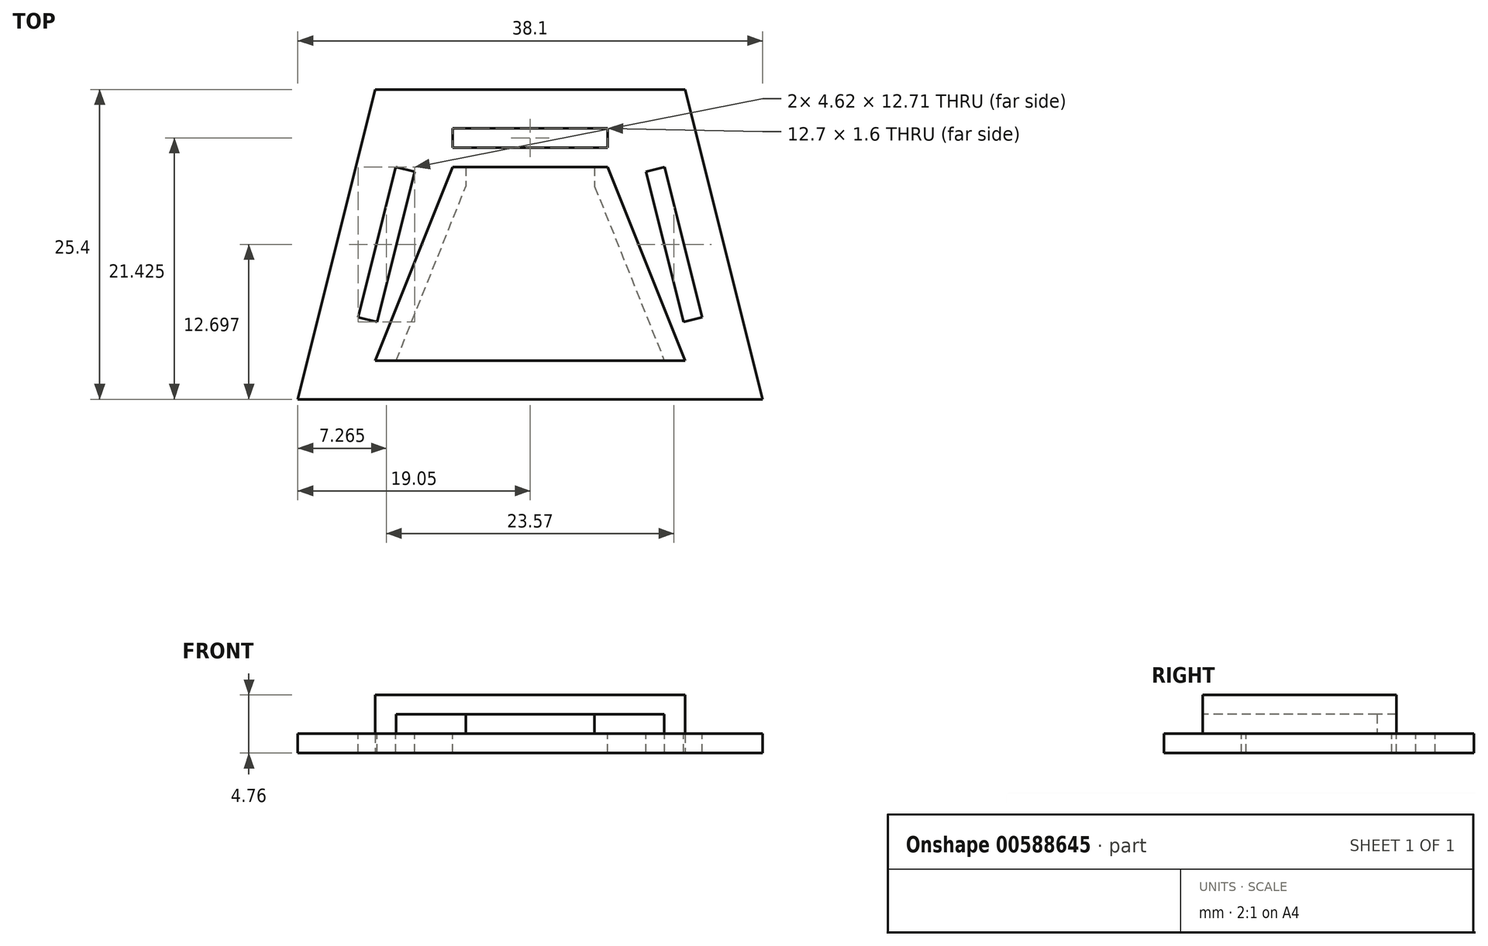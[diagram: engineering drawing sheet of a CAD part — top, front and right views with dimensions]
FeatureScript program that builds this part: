
annotation { "Feature Type Name" : "Feature", "Feature Type Description" : "" }
export const myFeature = defineFeature(function(context is Context, id is Id, definition is map)
    precondition{}
    {
        {
            var Q0;
            Q0=qCreatedBy(makeId("Top.planeOp"),FACE);
            var sketch = newSketch(context, id + "F0", { "sketchPlane" : qUnion([Q0])});
            skLineSegment(sketch, "E0", {"start": v(-19.05, -12.7) * mm, "end": v(19.05, -12.7) * mm});
            skLineSegment(sketch, "E1", {"start": v(-19.05, -12.7) * mm, "end": v(-12.7, 12.7) * mm});
            skLineSegment(sketch, "E2", {"start": v(-12.7, 12.7) * mm, "end": v(12.7, 12.7) * mm});
            skLineSegment(sketch, "E3", {"start": v(12.7, 12.7) * mm, "end": v(19.05, -12.7) * mm});
            skLineSegment(sketch, "E4", {"start": v(-19.05, -12.7) * mm, "end": v(-19.05, 12.7) * mm, "construction": true});
            skLineSegment(sketch, "E5", {"start": v(-19.05, 12.7) * mm, "end": v(-12.7, 12.7) * mm, "construction": true});
            skLineSegment(sketch, "E6", {"start": v(12.7, 12.7) * mm, "end": v(19.05, 12.7) * mm, "construction": true});
            skLineSegment(sketch, "E7", {"start": v(19.05, 12.7) * mm, "end": v(19.05, -12.7) * mm, "construction": true});
            skLineSegment(sketch, "E8", {"start": v(-19.05, -12.7) * mm, "end": v(19.05, 12.7) * mm, "construction": true});
            skPoint(sketch, "E9", {"position": v(0, 0) * mm});
            skSolve(sketch);
        }
        {
            var Q0;
            Q0 = qSketchRegion(id + "F0", true);
            extrude(context, id + "F1", {"entities" : qUnion([Q0]), "depth" : 1.59 * mm, "offsetDistance" : 25.4 * mm});
        }
        {
            var Q0;
            Q0=makeQuery(id+"F1.opExtrude","CAP_FACE",FACE,{"disambiguationData":[OSD([sQuery(id+"F0.wireOp",EDGE,"E0"),sQuery(id+"F0.wireOp",EDGE,"E1"),sQuery(id+"F0.wireOp",EDGE,"E2"),sQuery(id+"F0.wireOp",EDGE,"E3")])],"isStart":false});
            var sketch = newSketch(context, id + "F2", { "sketchPlane" : qUnion([Q0])});
            skLineSegment(sketch, "E10", {"start": v(-6.35, 6.35) * mm, "end": v(-12.7, -9.53) * mm});
            skLineSegment(sketch, "E11", {"start": v(-12.7, -9.53) * mm, "end": v(12.7, -9.53) * mm});
            skLineSegment(sketch, "E12", {"start": v(12.7, -9.53) * mm, "end": v(6.35, 6.35) * mm});
            skLineSegment(sketch, "E13", {"start": v(6.35, 6.35) * mm, "end": v(-6.35, 6.35) * mm});
            skSolve(sketch);
        }
        {
            var Q0;
            Q0 = qSketchRegion(id + "F2", true);
            extrude(context, id + "F3", {"entities" : qUnion([Q0]), "operationType" : NewBodyOperationType.ADD, "depth" : 3.17 * mm, "offsetDistance" : 25.4 * mm});
        }
        {
            var Q0;
            Q0=makeQuery(id+"F1.opExtrude","CAP_FACE",FACE,{"disambiguationData":[OSD([sQuery(id+"F0.wireOp",EDGE,"E0"),sQuery(id+"F0.wireOp",EDGE,"E1"),sQuery(id+"F0.wireOp",EDGE,"E2"),sQuery(id+"F0.wireOp",EDGE,"E3")])],"isStart":false});
            var sketch = newSketch(context, id + "F4", { "sketchPlane" : qUnion([Q0])});
            skLineSegment(sketch, "E14", {"start": v(9.47, 5.96) * mm, "end": v(11.01, 6.35) * mm});
            skLineSegment(sketch, "E15", {"start": v(11.01, 6.35) * mm, "end": v(14.1, -5.97) * mm});
            skLineSegment(sketch, "E16", {"start": v(14.1, -5.97) * mm, "end": v(12.55, -6.36) * mm});
            skLineSegment(sketch, "E17", {"start": v(12.55, -6.36) * mm, "end": v(9.47, 5.96) * mm});
            skLineSegment(sketch, "E18", {"start": v(0, 12.7) * mm, "end": v(0, -12.7) * mm, "construction": true});
            skPoint(sketch, "E18.endSnap0", {"position": v(0, 6.35) * mm});
            skLineSegment(sketch, "E19.MirrorCS", {"start": v(-12.55, -6.36) * mm, "end": v(-9.47, 5.96) * mm});
            skLineSegment(sketch, "E20.MirrorCS", {"start": v(-14.1, -5.97) * mm, "end": v(-12.55, -6.36) * mm});
            skLineSegment(sketch, "E21.MirrorCS", {"start": v(-9.47, 5.96) * mm, "end": v(-11.01, 6.35) * mm});
            skLineSegment(sketch, "E22.MirrorCS", {"start": v(-11.01, 6.35) * mm, "end": v(-14.1, -5.97) * mm});
            skLineSegment(sketch, "E23.bottom", {"start": v(6.35, 9.52) * mm, "end": v(-6.35, 9.52) * mm});
            skLineSegment(sketch, "E23.top", {"start": v(6.35, 7.92) * mm, "end": v(-6.35, 7.92) * mm});
            skLineSegment(sketch, "E23.left", {"start": v(6.35, 9.52) * mm, "end": v(6.35, 7.92) * mm});
            skLineSegment(sketch, "E23.right", {"start": v(-6.35, 9.52) * mm, "end": v(-6.35, 7.92) * mm});
            skPoint(sketch, "E23.middle", {"position": v(0, 8.72) * mm});
            skSolve(sketch);
        }
        {
            var Q0;
            Q0 = qSketchRegion(id + "F4", true);
            extrude(context, id + "F5", {"entities" : qUnion([Q0]), "operationType" : NewBodyOperationType.REMOVE, "endBound" : BoundingType.THROUGH_ALL, "oppositeDirection" : true, "depth" : 25.4 * mm, "offsetDistance" : 25.4 * mm});
        }
        {
            var Q0;
            Q0=makeQuery(id+"F3.opExtrude","SWEPT_FACE",FACE,{"disambiguationData":[OSD([sQuery(id+"F2.wireOp",EDGE,"E11")])]});
            shell(context, id + "F6", {"entities" : qUnion([Q0]), "thickness" : 1.59 * mm});
        }
        {
            var Q0;
            Q0=makeQuery(id+"F6.opShell","OFFSET_FACE",FACE,{"disambiguationData":[OSD([sQuery(id+"F2.wireOp",EDGE,"E13")])]});
            var sketch = newSketch(context, id + "F7", { "sketchPlane" : qUnion([Q0])});
            skLineSegment(sketch, "E24.bottom", {"start": v(-5.28, 1.59) * mm, "end": v(5.28, 1.59) * mm});
            skLineSegment(sketch, "E24.top", {"start": v(-5.28, 3.17) * mm, "end": v(5.28, 3.17) * mm});
            skLineSegment(sketch, "E24.left", {"start": v(-5.28, 1.59) * mm, "end": v(-5.28, 3.17) * mm});
            skLineSegment(sketch, "E24.right", {"start": v(5.28, 1.59) * mm, "end": v(5.28, 3.17) * mm});
            skSolve(sketch);
        }
        {
            var Q0;
            Q0 = qSketchRegion(id + "F7", true);
            extrude(context, id + "F8", {"entities" : qUnion([Q0]), "operationType" : NewBodyOperationType.REMOVE, "endBound" : BoundingType.THROUGH_ALL, "oppositeDirection" : true, "depth" : 25.4 * mm, "offsetDistance" : 25.4 * mm});
        }
    });
